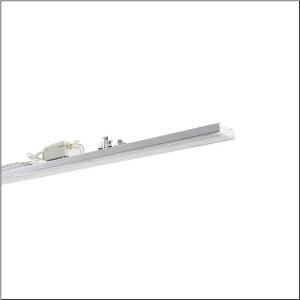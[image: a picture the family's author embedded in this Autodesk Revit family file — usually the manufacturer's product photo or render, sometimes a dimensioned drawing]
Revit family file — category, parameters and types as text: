
# Revit family: licross_r__11_recessed_ho_51tl11dv4m2s_9ec1
name_source: partatom
category: Lighting Fixtures
units: mm (PartAtom-declared; Revit-internal decimal feet)

## family parameters
Cut with Voids When Loaded = No
Host = Face
Light Source = No
Part Type = Normal
Room Calculation Point = No
Round Connector Dimension = Use Diameter
Shared = No

## types (1)
- --- (1 x LED, 27080 lm, 150.5 W, 4000K)
    Apparent Load = 150 VA
    CIE Flux Codes = 87 95 99 100 100
    Color Rendering = 80
    Color Temperature = 4000K
    Default Elevation = 1800 mm
    Description = Licross® 11 Recessed HO, luminaire insert, of sheet steel, coil coated, white, length: 2.250mm, width: 66mm, height: 67mm, LED rated luminous flux: 27.080lm, light colour: 840, control gear: DALI 2, with plug, 5-pole, with phase selection, mains connection: 220..240V, AC, 50/60Hz, rated input power: 151W, halogen-free wiring, primary light control with lens, of plastic, primary optical cover: cover, of PMMA, light emission: direct distribution, primary light characteristic: symmetric, protection rating (complete): IP40, insulation class (complete): insulation class I (protective earthing), certification: CE, ENEC, VDE, UKCA, protection symbol: D if used in an environment without relevant dust loads with corresponding accessories, impact resistance: IK06, permissible ambient temperature for indoor applications: -40..+35°C, corresponds to IFS (International Featured Standards) requirements for safety and quality in the food industry, reducing of maximum allowable ambient temperature of 5°C with ceiling mounting, LABS conformity tested according to VDMA 24364:2018-05, packaging unit: 1 piece
    Height = 58 mm
    Lamp = 1 x LED
    Lamp Light Flux = 27080 lm
    Lamp Power = 150.5 W
    Lamp count = 1
    Length = 2250 mm
    Luminous efficacy = 180 lm/W
    Manufacturer = Siteco
    ModVariant = No
    Model = 51TL11DV4M2S
    Mounting Place = Ceiling
    Mounting Type = Pendant
    Number of Poles = 1
    OnlyDefault = Yes
    Power Factor = 1
    Product Name = Licross® 11 Recessed HO
    Product group = luminaire insert
    ProductGroupID = 901
    Protection Class = Protection class I
    Protection Degree = IP 40
    RLX_Detail_Level = 1
    RLX_Emergency_Light_Flux = 0 lm
    RLX_Emergency_Type = 0
    RLX_Emergency_Type_DB = No
    RlxData = <blob elided: 29681 chars, md5=73948c6d>
    Socket = socket
    Standby Power = 0 W
    System Light Flux = 27079 lm
    System Power = 150 W
    Type Comments = factory setting: luminous flux: 100 % | dim-lin: 254 | 690 mA
    Type Image = l_1296930.jpg
    URL = http://relux.com
    VarID = @adj_067711
    Voltage = 0 V
    Weight = 0.00 kg
    Width = 66 mm

## geometry (parser evidence)
native form markers: Blend x4, Sweep x9
no freeform markers — native parametric forms only
